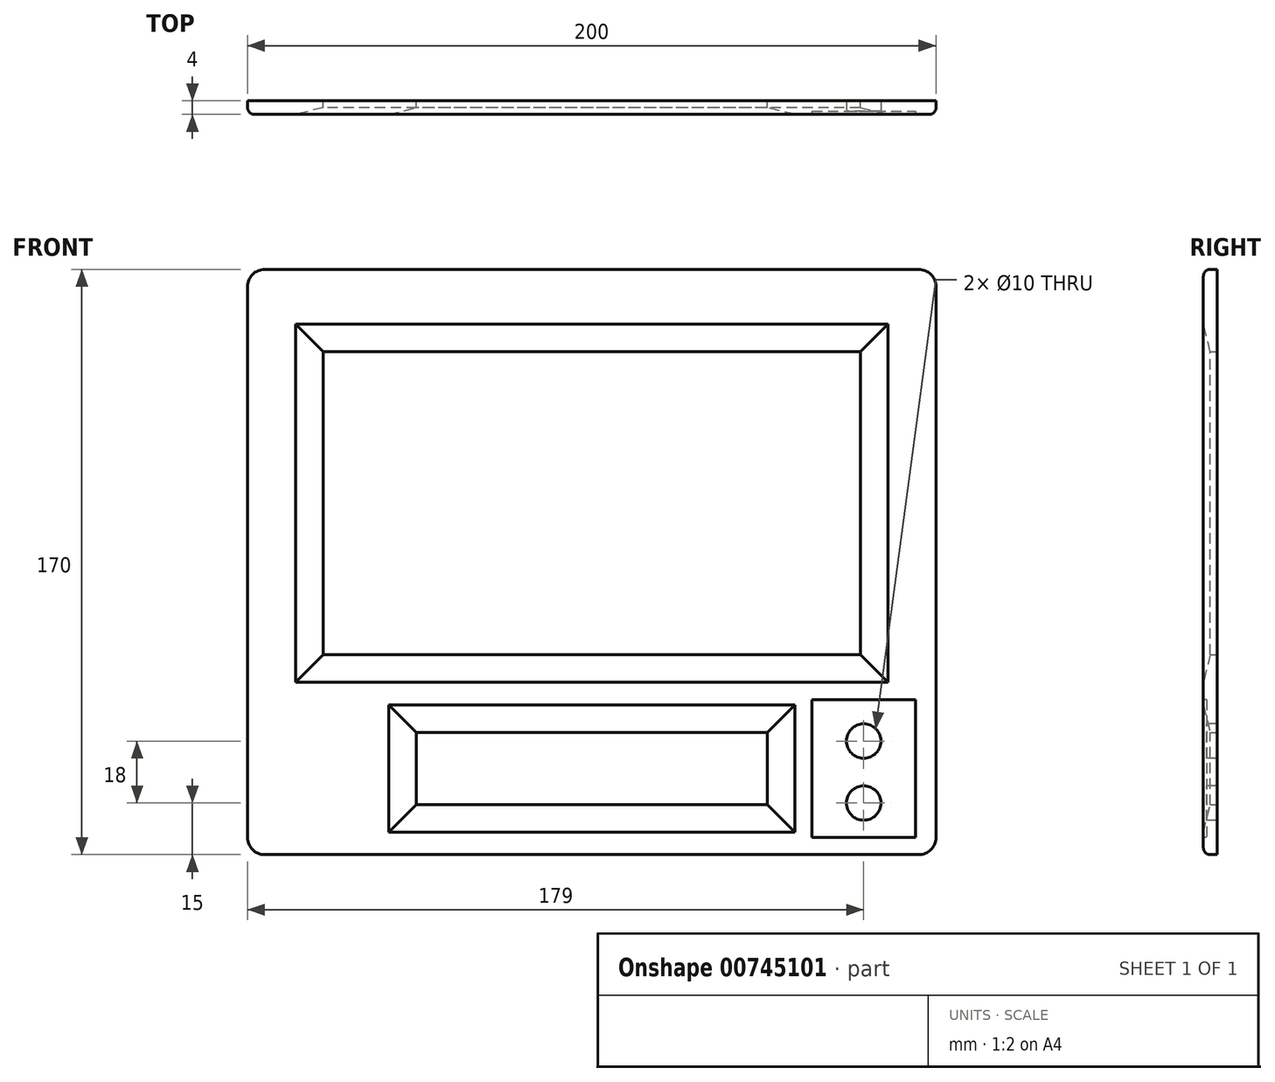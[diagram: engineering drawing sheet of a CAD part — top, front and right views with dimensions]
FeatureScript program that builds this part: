
annotation { "Feature Type Name" : "Feature", "Feature Type Description" : "" }
export const myFeature = defineFeature(function(context is Context, id is Id, definition is map)
    precondition{}
    {
        {
            var Q0;
            Q0=qCreatedBy(makeId("Front.planeOp"),FACE);
            var sketch = newSketch(context, id + "F0", { "sketchPlane" : qUnion([Q0])});
            skLineSegment(sketch, "E0.bottom", {"start": v(-100, 0) * mm, "end": v(100, 0) * mm});
            skLineSegment(sketch, "E0.top", {"start": v(-100, 170) * mm, "end": v(100, 170) * mm});
            skLineSegment(sketch, "E0.left", {"start": v(-100, 0) * mm, "end": v(-100, 170) * mm});
            skLineSegment(sketch, "E0.right", {"start": v(100, 0) * mm, "end": v(100, 170) * mm});
            skLineSegment(sketch, "E1.bottom", {"start": v(78, 146.15) * mm, "end": v(-78, 146.15) * mm});
            skLineSegment(sketch, "E1.top", {"start": v(78, 58.15) * mm, "end": v(-78, 58.15) * mm});
            skLineSegment(sketch, "E1.left", {"start": v(78, 146.15) * mm, "end": v(78, 58.15) * mm});
            skLineSegment(sketch, "E1.right", {"start": v(-78, 146.15) * mm, "end": v(-78, 58.15) * mm});
            skPoint(sketch, "E1.middle", {"position": v(0, 102.15) * mm});
            skLineSegment(sketch, "E2.bottom", {"start": v(51, 35.5) * mm, "end": v(-51, 35.5) * mm});
            skLineSegment(sketch, "E2.top", {"start": v(51, 14.5) * mm, "end": v(-51, 14.5) * mm});
            skLineSegment(sketch, "E2.left", {"start": v(51, 35.5) * mm, "end": v(51, 14.5) * mm});
            skLineSegment(sketch, "E2.right", {"start": v(-51, 35.5) * mm, "end": v(-51, 14.5) * mm});
            skPoint(sketch, "E2.middle", {"position": v(0, 25) * mm});
            skSolve(sketch);
        }
        {
            var Q0;
            Q0 = qSketchRegion(id + "F0", true);
            extrude(context, id + "F1", {"entities" : qUnion([Q0]), "depth" : 4 * mm, "offsetDistance" : 25 * mm});
        }
        {
            var Q0;
            Q0=makeQuery(id+"F1.opExtrude","SWEPT_EDGE",EDGE,{"disambiguationData":[OSD([sQuery(id+"F0.wireOp",EDGE,"E0.bottom"),sQuery(id+"F0.wireOp",EDGE,"E0.left")])]});
            fillet(context, id + "F2", {"entities" : qUnion([Q0]), "radius" : 5 * mm, "tangentPropagation" : true, "allowEdgeOverflow" : false});
        }
        {
            var Q0;
            Q0=makeQuery(id+"F1.opExtrude","SWEPT_EDGE",EDGE,{"disambiguationData":[OSD([sQuery(id+"F0.wireOp",EDGE,"E0.bottom"),sQuery(id+"F0.wireOp",EDGE,"E0.right")])]});
            var Q1;
            Q1=makeQuery(id+"F1.opExtrude","SWEPT_EDGE",EDGE,{"disambiguationData":[OSD([sQuery(id+"F0.wireOp",EDGE,"E0.top"),sQuery(id+"F0.wireOp",EDGE,"E0.right")])]});
            var Q2;
            Q2=makeQuery(id+"F1.opExtrude","SWEPT_EDGE",EDGE,{"disambiguationData":[OSD([sQuery(id+"F0.wireOp",EDGE,"E0.top"),sQuery(id+"F0.wireOp",EDGE,"E0.left")])]});
            fillet(context, id + "F3", {"entities" : qUnion([Q0, Q1, Q2]), "radius" : 5 * mm, "tangentPropagation" : true, "allowEdgeOverflow" : false});
        }
        {
            var Q0;
            Q0=makeQuery(id+"F1.opExtrude","CAP_EDGE",EDGE,{"disambiguationData":[OSD([sQuery(id+"F0.wireOp",EDGE,"E1.right")])],"isStart":false});
            var Q1;
            Q1=makeQuery(id+"F1.opExtrude","CAP_EDGE",EDGE,{"disambiguationData":[OSD([sQuery(id+"F0.wireOp",EDGE,"E1.left")])],"isStart":false});
            var Q2;
            Q2=makeQuery(id+"F1.opExtrude","CAP_EDGE",EDGE,{"disambiguationData":[OSD([sQuery(id+"F0.wireOp",EDGE,"E1.bottom")])],"isStart":false});
            var Q3;
            Q3=makeQuery(id+"F1.opExtrude","CAP_EDGE",EDGE,{"disambiguationData":[OSD([sQuery(id+"F0.wireOp",EDGE,"E1.top")])],"isStart":false});
            var Q4;
            Q4=makeQuery(id+"F1.opExtrude","CAP_EDGE",EDGE,{"disambiguationData":[OSD([sQuery(id+"F0.wireOp",EDGE,"E2.bottom")])],"isStart":false});
            var Q5;
            Q5=makeQuery(id+"F1.opExtrude","CAP_EDGE",EDGE,{"disambiguationData":[OSD([sQuery(id+"F0.wireOp",EDGE,"E2.top")])],"isStart":false});
            var Q6;
            Q6=makeQuery(id+"F1.opExtrude","CAP_EDGE",EDGE,{"disambiguationData":[OSD([sQuery(id+"F0.wireOp",EDGE,"E2.right")])],"isStart":false});
            var Q7;
            Q7=makeQuery(id+"F1.opExtrude","CAP_EDGE",EDGE,{"disambiguationData":[OSD([sQuery(id+"F0.wireOp",EDGE,"E2.left")])],"isStart":false});
            chamfer(context, id + "F4", {"entities" : qUnion([Q0, Q1, Q2, Q3, Q4, Q5, Q6, Q7]), "chamferType" : ChamferType.TWO_OFFSETS, "width1" : 2 * mm, "oppositeDirection" : false, "width2" : 8 * mm, "tangentPropagation" : true});
        }
        {
            var Q0;
            Q0=makeQuery(id+"F1.opExtrude","CAP_EDGE",EDGE,{"disambiguationData":[OSD([sQuery(id+"F0.wireOp",EDGE,"E0.bottom")])],"isStart":false});
            fillet(context, id + "F5", {"entities" : qUnion([Q0]), "radius" : 2 * mm, "tangentPropagation" : true, "allowEdgeOverflow" : false});
        }
        {
            var Q0;
            Q0=makeQuery(id+"F1.opExtrude","CAP_FACE",FACE,{"disambiguationData":[OSD([sQuery(id+"F0.wireOp",EDGE,"E0.bottom"),sQuery(id+"F0.wireOp",EDGE,"E0.top"),sQuery(id+"F0.wireOp",EDGE,"E0.left"),sQuery(id+"F0.wireOp",EDGE,"E0.right"),sQuery(id+"F0.wireOp",EDGE,"E1.bottom"),sQuery(id+"F0.wireOp",EDGE,"E1.top"),sQuery(id+"F0.wireOp",EDGE,"E1.left"),sQuery(id+"F0.wireOp",EDGE,"E1.right"),sQuery(id+"F0.wireOp",EDGE,"E2.bottom"),sQuery(id+"F0.wireOp",EDGE,"E2.top"),sQuery(id+"F0.wireOp",EDGE,"E2.left"),sQuery(id+"F0.wireOp",EDGE,"E2.right")])],"isStart":false});
            var sketch = newSketch(context, id + "F6", { "sketchPlane" : qUnion([Q0])});
            skLineSegment(sketch, "E3.bottom", {"start": v(64, 45) * mm, "end": v(94, 45) * mm});
            skLineSegment(sketch, "E3.top", {"start": v(64, 5) * mm, "end": v(94, 5) * mm});
            skLineSegment(sketch, "E3.left", {"start": v(64, 45) * mm, "end": v(64, 5) * mm});
            skLineSegment(sketch, "E3.right", {"start": v(94, 45) * mm, "end": v(94, 5) * mm});
            skSolve(sketch);
        }
        {
            var Q0;
            Q0 = qSketchRegion(id + "F6", true);
            extrude(context, id + "F7", {"entities" : qUnion([Q0]), "operationType" : NewBodyOperationType.REMOVE, "oppositeDirection" : true, "depth" : 1 * mm, "offsetDistance" : 25 * mm});
        }
        {
            var Q0;
            Q0=makeQuery(id+"F7.boolean.opBoolean","COPY",FACE,{"derivedFrom":makeQuery(id+"F7.opExtrude","CAP_FACE",FACE,{"disambiguationData":[OSD([sQuery(id+"F6.wireOp",EDGE,"E3.bottom"),sQuery(id+"F6.wireOp",EDGE,"E3.top"),sQuery(id+"F6.wireOp",EDGE,"E3.left"),sQuery(id+"F6.wireOp",EDGE,"E3.right")])],"isStart":false})});
            var sketch = newSketch(context, id + "F8", { "sketchPlane" : qUnion([Q0])});
            skCircle(sketch, "E4", {"center": v(79, 15) * mm, "radius": 5 * mm});
            skCircle(sketch, "E5", {"center": v(79, 33) * mm, "radius": 5 * mm});
            skSolve(sketch);
        }
        {
            var Q0;
            Q0 = qSketchRegion(id + "F8", true);
            extrude(context, id + "F9", {"entities" : qUnion([Q0]), "operationType" : NewBodyOperationType.REMOVE, "oppositeDirection" : true, "depth" : 25 * mm, "offsetDistance" : 25 * mm});
        }
    });
